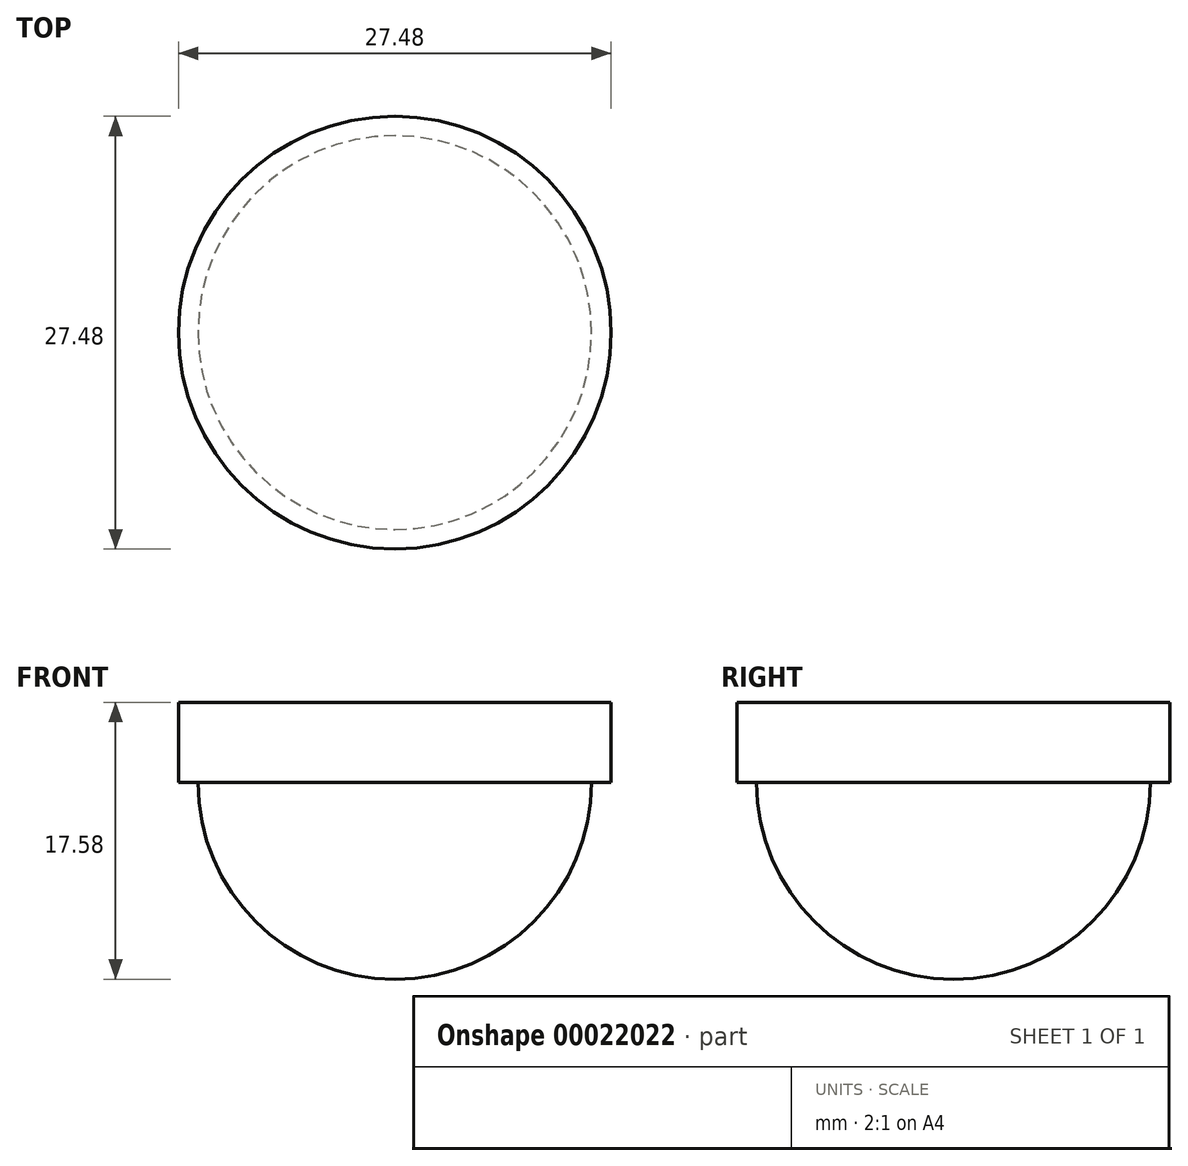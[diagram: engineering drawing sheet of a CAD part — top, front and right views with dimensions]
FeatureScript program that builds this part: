
annotation { "Feature Type Name" : "Feature", "Feature Type Description" : "" }
export const myFeature = defineFeature(function(context is Context, id is Id, definition is map)
    precondition{}
    {
        {
            var Q0;
            Q0=qCreatedBy(makeId("Top.planeOp"),FACE);
            var sketch = newSketch(context, id + "F0", { "sketchPlane" : qUnion([Q0])});
            skCircle(sketch, "E0", {"center": v(0, 0) * mm, "radius": 12.5 * mm});
            skLineSegment(sketch, "E1", {"start": v(0, 0) * mm, "end": v(12.5, 0) * mm});
            skLineSegment(sketch, "E2", {"start": v(0, 0) * mm, "end": v(-12.5, 0) * mm});
            skSolve(sketch);
        }
        {
            var Q0;
            {var subQ1=sQuery(id+"F0.wireOp",EDGE,"E1");Q0=makeQuery(id+"F0.imprint","IMPRINT",FACE,{"disambiguationData":[TD([[makeQuery(id+"F0.imprint","IMPRINT",EDGE,{"derivedFrom":subQ1}),-1.0]])]});}
            var Q1;
            Q1=sQuery(id+"F0.wireOp",EDGE,"E2");
            revolve(context, id + "F1", {"entities" : qUnion([Q0]), "axis" : qUnion([Q1]), "revolveType" : RevolveType.ONE_DIRECTION, "oppositeDirection" : true, "angle" : 180 * degree});
        }
        {
            var Q0;
            Q0=makeQuery(id+"F1.opRevolve","CAP_FACE",FACE,{"disambiguationData":[OSD([sQuery(id+"F0.wireOp",EDGE,"E0"),sQuery(id+"F0.wireOp",EDGE,"E1"),sQuery(id+"F0.wireOp",EDGE,"E2")])],"isStart":false});
            var sketch = newSketch(context, id + "F2", { "sketchPlane" : qUnion([Q0])});
            skCircle(sketch, "E3", {"center": v(0, 0) * mm, "radius": 13.74 * mm});
            skSolve(sketch);
        }
        {
            var Q0;
            Q0 = qSketchRegion(id + "F2", true);
            extrude(context, id + "F3", {"entities" : qUnion([Q0]), "operationType" : NewBodyOperationType.ADD, "depth" : 5.08 * mm});
        }
    });
